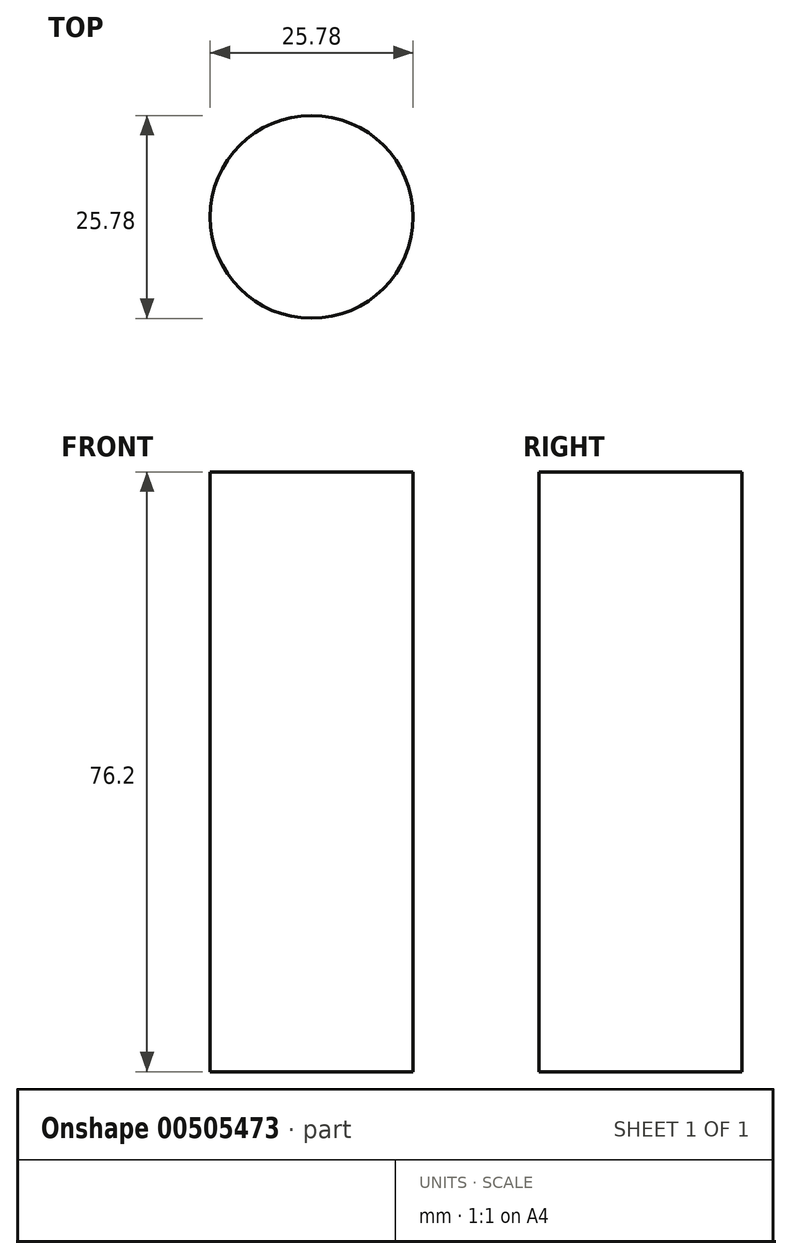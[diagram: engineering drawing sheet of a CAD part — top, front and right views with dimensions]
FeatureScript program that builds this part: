
annotation { "Feature Type Name" : "Feature", "Feature Type Description" : "" }
export const myFeature = defineFeature(function(context is Context, id is Id, definition is map)
    precondition{}
    {
        {
            var Q0;
            Q0=qCreatedBy(makeId("Top.planeOp"),FACE);
            var sketch = newSketch(context, id + "F0", { "sketchPlane" : qUnion([Q0])});
            skCircle(sketch, "E0", {"center": v(0, 0) * mm, "radius": 12.89 * mm});
            skSolve(sketch);
        }
        {
            var Q0;
            Q0=makeQuery(id+"F0.imprint","IMPRINT",FACE,{"disambiguationData":[TD([[makeQuery(id+"F0.imprint","IMPRINT",EDGE,{"derivedFrom":sQuery(id+"F0.wireOp",EDGE,"E0")}),1.0]])]});
            extrude(context, id + "F1", {"entities" : qUnion([Q0]), "depth" : 76.2 * mm});
        }
    });
